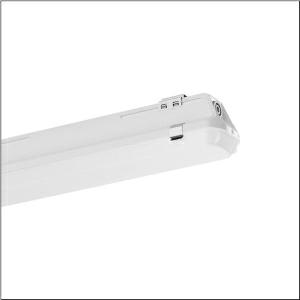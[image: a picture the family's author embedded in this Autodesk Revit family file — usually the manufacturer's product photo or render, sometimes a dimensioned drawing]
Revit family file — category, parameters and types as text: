
# Revit family: monsun_r__21_parking_51fg20dp440bhq_097c
name_source: partatom
category: Lighting Fixtures
units: mm (PartAtom-declared; Revit-internal decimal feet)

## family parameters
Cut with Voids When Loaded = No
Host = Face
Light Source = No
Part Type = Normal
Room Calculation Point = No
Round Connector Dimension = Use Diameter
Shared = No

## types (1)
- --- (1 x LED, 4810 lm, 34.9 W, 4000K)
    Apparent Load = 35 VA
    CIE Flux Codes = 45 75 93 94 100
    Color Rendering = 80
    Color Temperature = 4000K
    Default Elevation = 1800 mm
    Description = Monsun® 21 parking, damp-proof luminaire, chain hanger, primary optical cover: enclosure, of PC, light emission: direct distribution, primary light characteristic: symmetric, installation type: suspended mounting, surface-mounted, horizontal mounting, vertical mounting, LED, rated luminous flux: 4.810lm, luminous efficacy: 140lm/W, light colour: 840, colour temperature: 4000K, control gear: ECG DALI, with terminal, 5-pole, max. 2.5mm², mains connection: 220..240V, AC, 50/60Hz, rated input power: 34W, housing, of glass-fibre reinforced polyester, uncoated, bright grey, incl. chain hanger, length: 1.590mm, width: 90mm, height: 88mm, clip for enclosure, of stainless steel (V2A), ceiling mounting element, of stainless steel (V2A), chain hanger, of stainless steel (V2A), multi-sensor HC1, local controlcentral control, scope of services: certified according to part 101,103,303,304, dimmable, protection rating (complete): IP66, insulation class (complete): insulation class I (protective earthing), certification: CE, ENEC, VDE, UKCA, protection symbol: D, impact resistance: IK08, permissible operating ambient temperature: -25..+35°C, standard: EN 50419, EN 60598-2-1, corresponds to IFS (International Featured Standards) requirements for safety and quality in the food industry, for indoor or canopied outdoor use, no direct snow, no direct sun, no direct rain, contact your sales advisor before using the luminaires in applications with unclear chemical exposure, large temperature fluctuations or condensation-forming humidity, LABS conformity tested according to VDMA 24364:2018-05, packaging unit: 1 piece
    Height = 89 mm
    Lamp = 1 x LED
    Lamp Light Flux = 4810 lm
    Lamp Power = 34.9 W
    Lamp count = 1
    Length = 1590 mm
    Luminous efficacy = 138 lm/W
    Manufacturer = Siteco
    ModVariant = No
    Model = 51FG20DP440BHQ
    Mounting Place = Ceiling
    Mounting Type = Surface mounted
    Number of Poles = 1
    OnlyDefault = Yes
    Power Factor = 1
    Product Name = Monsun® 21 parking
    Product group = damp-proof luminaire
    ProductGroupID = 301
    Protection Class = Protection class I
    Protection Degree = IP 66
    RLX_Detail_Level = 1
    RLX_Emergency_Light_Flux = 0 lm
    RLX_Emergency_Type = 0
    RLX_Emergency_Type_DB = No
    RlxData = <blob elided: 91969 chars, md5=be0b3ace>
    Socket = socket
    Standby Power = 0 W
    System Light Flux = 4810 lm
    System Power = 35 W
    Type Comments = factory setting: luminous flux: 100 % | dim-lin: 254 | 228 mA
    Type Image = l_1006717.jpg
    URL = http://relux.com
    VarID = @adj_092839
    Voltage = 0 V
    Weight = 0.00 kg
    Width = 90 mm

## geometry (parser evidence)
native form markers: Blend x4, Sweep x13
no freeform markers — native parametric forms only
